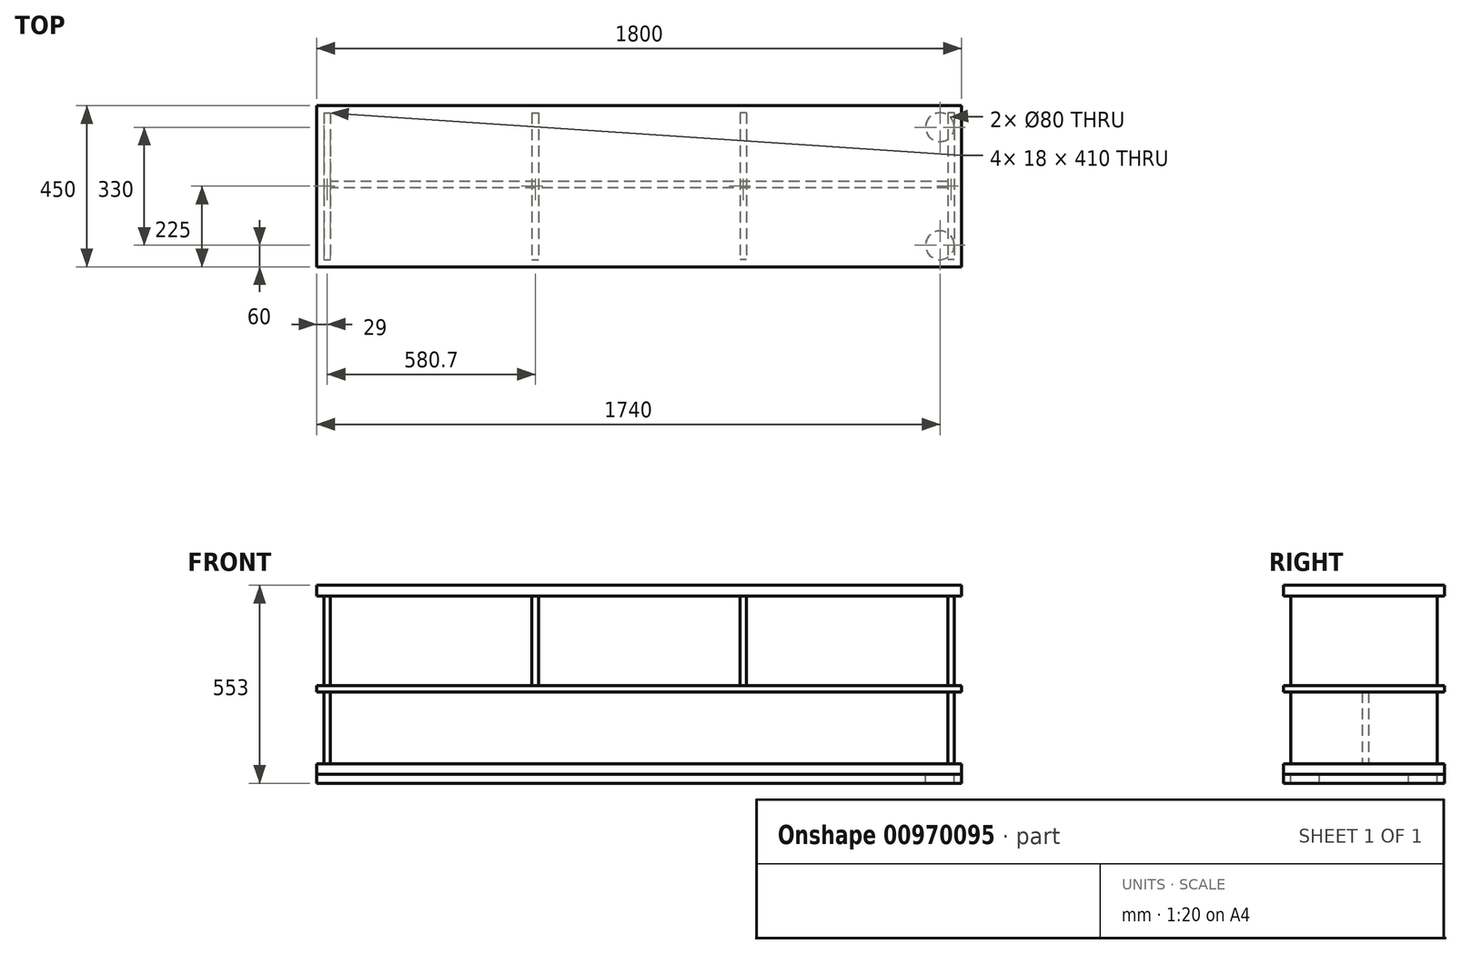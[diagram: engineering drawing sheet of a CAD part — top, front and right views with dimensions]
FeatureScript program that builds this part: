
annotation { "Feature Type Name" : "Feature", "Feature Type Description" : "" }
export const myFeature = defineFeature(function(context is Context, id is Id, definition is map)
    precondition{}
    {
        {
            var Q0;
            Q0=qCreatedBy(makeId("Top.planeOp"),FACE);
            var sketch = newSketch(context, id + "F0", { "sketchPlane" : qUnion([Q0])});
            skLineSegment(sketch, "E0.bottom", {"start": v(0, 0) * mm, "end": v(1800, 0) * mm});
            skLineSegment(sketch, "E0.top", {"start": v(0, 450) * mm, "end": v(1800, 450) * mm});
            skLineSegment(sketch, "E0.left", {"start": v(0, 0) * mm, "end": v(0, 450) * mm});
            skLineSegment(sketch, "E0.right", {"start": v(1800, 0) * mm, "end": v(1800, 450) * mm});
            skSolve(sketch);
        }
        {
            var Q0;
            Q0=makeQuery(id+"F0.imprint","IMPRINT",FACE,{"disambiguationData":[TD([[makeQuery(id+"F0.imprint","IMPRINT",EDGE,{"derivedFrom":sQuery(id+"F0.wireOp",EDGE,"E0.bottom")}),1.0]])]});
            var Q1;
            Q1=sQuery(id+"F0.wireOp",EDGE,"E0.left");
            var Q2;
            Q2=sQuery(id+"F0.wireOp",EDGE,"E0.top");
            var Q3;
            Q3=sQuery(id+"F0.wireOp",EDGE,"E0.bottom");
            var Q4;
            Q4=sQuery(id+"F0.wireOp",EDGE,"E0.right");
            extrude(context, id + "F1", {"entities" : qUnion([Q0]), "surfaceEntities" : qUnion([Q1, Q2, Q3, Q4]), "depth" : 30 * mm, "offsetDistance" : 25 * mm});
        }
        {
            var Q0;
            Q0=makeQuery(id+"F1.opExtrude","CAP_FACE",FACE,{"disambiguationData":[OSD([sQuery(id+"F0.wireOp",EDGE,"E0.bottom"),sQuery(id+"F0.wireOp",EDGE,"E0.top"),sQuery(id+"F0.wireOp",EDGE,"E0.left"),sQuery(id+"F0.wireOp",EDGE,"E0.right")])],"isStart":false});
            var sketch = newSketch(context, id + "F2", { "sketchPlane" : qUnion([Q0])});
            skLineSegment(sketch, "E1.bottom", {"start": v(20, 430) * mm, "end": v(38, 430) * mm});
            skLineSegment(sketch, "E1.top", {"start": v(20, 20) * mm, "end": v(38, 20) * mm});
            skLineSegment(sketch, "E1.left", {"start": v(20, 430) * mm, "end": v(20, 20) * mm});
            skLineSegment(sketch, "E1.right", {"start": v(38, 430) * mm, "end": v(38, 20) * mm});
            skLineSegment(sketch, "E2", {"start": v(900, 450) * mm, "end": v(900, 0) * mm, "construction": true});
            skLineSegment(sketch, "E3.MirrorCS", {"start": v(1762, 430) * mm, "end": v(1762, 20) * mm});
            skLineSegment(sketch, "E4.MirrorCS", {"start": v(1780, 430) * mm, "end": v(1780, 20) * mm});
            skLineSegment(sketch, "E5.MirrorCS", {"start": v(1780, 430) * mm, "end": v(1762, 430) * mm});
            skLineSegment(sketch, "E6.MirrorCS", {"start": v(1780, 20) * mm, "end": v(1762, 20) * mm});
            skSolve(sketch);
        }
        {
            var Q0;
            Q0=makeQuery(id+"F2.imprint","IMPRINT",FACE,{"disambiguationData":[TD([[makeQuery(id+"F2.imprint","IMPRINT",EDGE,{"derivedFrom":sQuery(id+"F2.wireOp",EDGE,"E1.bottom")}),-1.0]])]});
            var Q1;
            Q1=makeQuery(id+"F2.imprint","IMPRINT",FACE,{"disambiguationData":[TD([[makeQuery(id+"F2.imprint","IMPRINT",EDGE,{"derivedFrom":sQuery(id+"F2.wireOp",EDGE,"E5.MirrorCS")}),1.0]])]});
            extrude(context, id + "F3", {"entities" : qUnion([Q0, Q1]), "depth" : 200 * mm, "offsetDistance" : 25 * mm});
        }
        {
            var Q0;
            Q0=makeQuery(id+"F3.opExtrude","SWEPT_FACE",FACE,{"disambiguationData":[OSD([sQuery(id+"F2.wireOp",EDGE,"E1.right")])]});
            var sketch = newSketch(context, id + "F4", { "sketchPlane" : qUnion([Q0])});
            skLineSegment(sketch, "E7.bottom", {"start": v(220, 230) * mm, "end": v(238, 230) * mm});
            skLineSegment(sketch, "E7.top", {"start": v(220, 30) * mm, "end": v(238, 30) * mm});
            skLineSegment(sketch, "E7.left", {"start": v(220, 230) * mm, "end": v(220, 30) * mm});
            skLineSegment(sketch, "E7.right", {"start": v(238, 230) * mm, "end": v(238, 30) * mm});
            skSolve(sketch);
        }
        {
            var Q0;
            Q0=makeQuery(id+"F4.imprint","IMPRINT",FACE,{"disambiguationData":[TD([[makeQuery(id+"F4.imprint","IMPRINT",EDGE,{"derivedFrom":sQuery(id+"F4.wireOp",EDGE,"E7.bottom")}),1.0]])]});
            extrude(context, id + "F5", {"entities" : qUnion([Q0]), "depth" : 1724 * mm, "offsetDistance" : 25 * mm});
        }
        {
            var Q0;
            Q0=qCreatedBy(makeId("Top.planeOp"),FACE);
            cPlane(context, id + "F6", {"entities" : qUnion([Q0]), "cplaneType" : CPlaneType.OFFSET, "offset" : 230 * mm, "width" : 150 * mm, "height" : 150 * mm});
        }
        {
            var Q0;
            Q0=qCreatedBy(id+"F6.planeOp",FACE);
            var sketch = newSketch(context, id + "F7", { "sketchPlane" : qUnion([Q0])});
            skLineSegment(sketch, "E8.bottom", {"start": v(0, 0) * mm, "end": v(1800, 0) * mm});
            skLineSegment(sketch, "E8.top", {"start": v(0, 450) * mm, "end": v(1800, 450) * mm});
            skLineSegment(sketch, "E8.left", {"start": v(0, 0) * mm, "end": v(0, 450) * mm});
            skLineSegment(sketch, "E8.right", {"start": v(1800, 0) * mm, "end": v(1800, 450) * mm});
            skSolve(sketch);
        }
        {
            var Q0;
            Q0=makeQuery(id+"F7.imprint","IMPRINT",FACE,{"disambiguationData":[TD([[makeQuery(id+"F7.imprint","IMPRINT",EDGE,{"derivedFrom":sQuery(id+"F7.wireOp",EDGE,"E8.bottom")}),1.0]])]});
            extrude(context, id + "F8", {"entities" : qUnion([Q0]), "depth" : 18 * mm, "offsetDistance" : 25 * mm});
        }
        {
            var Q0;
            Q0=makeQuery(id+"F8.opExtrude","CAP_FACE",FACE,{"disambiguationData":[OSD([sQuery(id+"F7.wireOp",EDGE,"E8.bottom"),sQuery(id+"F7.wireOp",EDGE,"E8.top"),sQuery(id+"F7.wireOp",EDGE,"E8.left"),sQuery(id+"F7.wireOp",EDGE,"E8.right")])],"isStart":false});
            var sketch = newSketch(context, id + "F9", { "sketchPlane" : qUnion([Q0])});
            skLineSegment(sketch, "E9.bottom", {"start": v(20, 430) * mm, "end": v(38, 430) * mm});
            skLineSegment(sketch, "E9.top", {"start": v(20, 20) * mm, "end": v(38, 20) * mm});
            skLineSegment(sketch, "E9.left", {"start": v(20, 430) * mm, "end": v(20, 20) * mm});
            skLineSegment(sketch, "E9.right", {"start": v(38, 430) * mm, "end": v(38, 20) * mm});
            skLineSegment(sketch, "E10.bottom", {"start": v(600.7, 430) * mm, "end": v(618.7, 430) * mm});
            skLineSegment(sketch, "E10.top", {"start": v(600.7, 20) * mm, "end": v(618.7, 20) * mm});
            skLineSegment(sketch, "E10.left", {"start": v(600.7, 430) * mm, "end": v(600.7, 20) * mm});
            skLineSegment(sketch, "E10.right", {"start": v(618.7, 430) * mm, "end": v(618.7, 20) * mm});
            skLineSegment(sketch, "E11", {"start": v(900, 0) * mm, "end": v(900, 450) * mm, "construction": true});
            skLineSegment(sketch, "E12.MirrorCS", {"start": v(1762, 430) * mm, "end": v(1762, 20) * mm});
            skLineSegment(sketch, "E13.MirrorCS", {"start": v(1780, 430) * mm, "end": v(1780, 20) * mm});
            skLineSegment(sketch, "E14.MirrorCS", {"start": v(1199.3, 20) * mm, "end": v(1181.3, 20) * mm});
            skLineSegment(sketch, "E15.MirrorCS", {"start": v(1780, 430) * mm, "end": v(1762, 430) * mm});
            skLineSegment(sketch, "E16.MirrorCS", {"start": v(1780, 20) * mm, "end": v(1762, 20) * mm});
            skLineSegment(sketch, "E17.MirrorCS", {"start": v(1199.3, 430) * mm, "end": v(1181.3, 430) * mm});
            skLineSegment(sketch, "E18.MirrorCS", {"start": v(1199.3, 430) * mm, "end": v(1199.3, 20) * mm});
            skLineSegment(sketch, "E19.MirrorCS", {"start": v(1181.3, 430) * mm, "end": v(1181.3, 20) * mm});
            skSolve(sketch);
        }
        {
            var Q0;
            Q0=makeQuery(id+"F9.imprint","IMPRINT",FACE,{"disambiguationData":[TD([[makeQuery(id+"F9.imprint","IMPRINT",EDGE,{"derivedFrom":sQuery(id+"F9.wireOp",EDGE,"E15.MirrorCS")}),1.0]])]});
            var Q1;
            Q1=makeQuery(id+"F9.imprint","IMPRINT",FACE,{"disambiguationData":[TD([[makeQuery(id+"F9.imprint","IMPRINT",EDGE,{"derivedFrom":sQuery(id+"F9.wireOp",EDGE,"E10.bottom")}),-1.0]])]});
            var Q2;
            Q2=makeQuery(id+"F9.imprint","IMPRINT",FACE,{"disambiguationData":[TD([[makeQuery(id+"F9.imprint","IMPRINT",EDGE,{"derivedFrom":sQuery(id+"F9.wireOp",EDGE,"E14.MirrorCS")}),-1.0]])]});
            var Q3;
            Q3=makeQuery(id+"F9.imprint","IMPRINT",FACE,{"disambiguationData":[TD([[makeQuery(id+"F9.imprint","IMPRINT",EDGE,{"derivedFrom":sQuery(id+"F9.wireOp",EDGE,"E9.bottom")}),-1.0]])]});
            extrude(context, id + "F10", {"entities" : qUnion([Q0, Q1, Q2, Q3]), "operationType" : NewBodyOperationType.ADD, "depth" : 250 * mm, "offsetDistance" : 25 * mm});
        }
        {
            var Q0;
            Q0=qCreatedBy(id+"F6.planeOp",FACE);
            cPlane(context, id + "F11", {"entities" : qUnion([Q0]), "cplaneType" : CPlaneType.OFFSET, "offset" : 268 * mm, "width" : 150 * mm, "height" : 150 * mm});
        }
        {
            var Q0;
            Q0=qCreatedBy(id+"F11.planeOp",FACE);
            var sketch = newSketch(context, id + "F12", { "sketchPlane" : qUnion([Q0])});
            skLineSegment(sketch, "E20.bottom", {"start": v(0, 0) * mm, "end": v(1800, 0) * mm});
            skLineSegment(sketch, "E20.top", {"start": v(0, 450) * mm, "end": v(1800, 450) * mm});
            skLineSegment(sketch, "E20.left", {"start": v(0, 0) * mm, "end": v(0, 450) * mm});
            skLineSegment(sketch, "E20.right", {"start": v(1800, 0) * mm, "end": v(1800, 450) * mm});
            skSolve(sketch);
        }
        {
            var Q0;
            Q0 = qSketchRegion(id + "F12", true);
            extrude(context, id + "F13", {"entities" : qUnion([Q0]), "operationType" : NewBodyOperationType.ADD, "depth" : 30 * mm, "offsetDistance" : 25 * mm});
        }
        {
            var Q0;
            Q0=makeQuery(id+"F1.opExtrude","CAP_FACE",FACE,{"disambiguationData":[OSD([sQuery(id+"F0.wireOp",EDGE,"E0.bottom"),sQuery(id+"F0.wireOp",EDGE,"E0.top"),sQuery(id+"F0.wireOp",EDGE,"E0.left"),sQuery(id+"F0.wireOp",EDGE,"E0.right")])],"isStart":true});
            var sketch = newSketch(context, id + "F14", { "sketchPlane" : qUnion([Q0])});
            skCircle(sketch, "E21", {"center": v(60, -390) * mm, "radius": 40 * mm});
            skCircle(sketch, "E22", {"center": v(60, -60) * mm, "radius": 40 * mm});
            skLineSegment(sketch, "E23", {"start": v(900, -450) * mm, "end": v(900, 0) * mm, "construction": true});
            skCircle(sketch, "E24.MirrorC", {"center": v(1740, -60) * mm, "radius": 40 * mm});
            skCircle(sketch, "E25.MirrorC", {"center": v(1740, -390) * mm, "radius": 40 * mm});
            skSolve(sketch);
        }
        {
            var Q0;
            Q0=makeQuery(id+"F14.imprint","IMPRINT",FACE,{"disambiguationData":[TD([[makeQuery(id+"F14.imprint","IMPRINT",EDGE,{"derivedFrom":sQuery(id+"F14.wireOp",EDGE,"E21")}),1.0]])]});
            var Q1;
            Q1=makeQuery(id+"F14.imprint","IMPRINT",FACE,{"disambiguationData":[TD([[makeQuery(id+"F14.imprint","IMPRINT",EDGE,{"derivedFrom":sQuery(id+"F14.wireOp",EDGE,"E22")}),1.0]])]});
            var Q2;
            Q2=makeQuery(id+"F14.imprint","IMPRINT",FACE,{"disambiguationData":[TD([[makeQuery(id+"F14.imprint","IMPRINT",EDGE,{"derivedFrom":sQuery(id+"F14.wireOp",EDGE,"E25.MirrorC")}),-1.0]])]});
            var Q3;
            Q3=makeQuery(id+"F14.imprint","IMPRINT",FACE,{"disambiguationData":[TD([[makeQuery(id+"F14.imprint","IMPRINT",EDGE,{"derivedFrom":sQuery(id+"F14.wireOp",EDGE,"E24.MirrorC")}),-1.0]])]});
            var Q4;
            Q4=sQuery(id+"F14.wireOp",EDGE,"E22");
            var Q5;
            Q5=sQuery(id+"F14.wireOp",EDGE,"E21");
            var Q6;
            Q6=sQuery(id+"F14.wireOp",EDGE,"E25.MirrorC");
            var Q7;
            Q7=sQuery(id+"F14.wireOp",EDGE,"E24.MirrorC");
            extrude(context, id + "F15", {"entities" : qUnion([Q0, Q1, Q2, Q3]), "surfaceEntities" : qUnion([Q4, Q5, Q6, Q7]), "depth" : 25 * mm, "offsetDistance" : 25 * mm});
        }
    });
